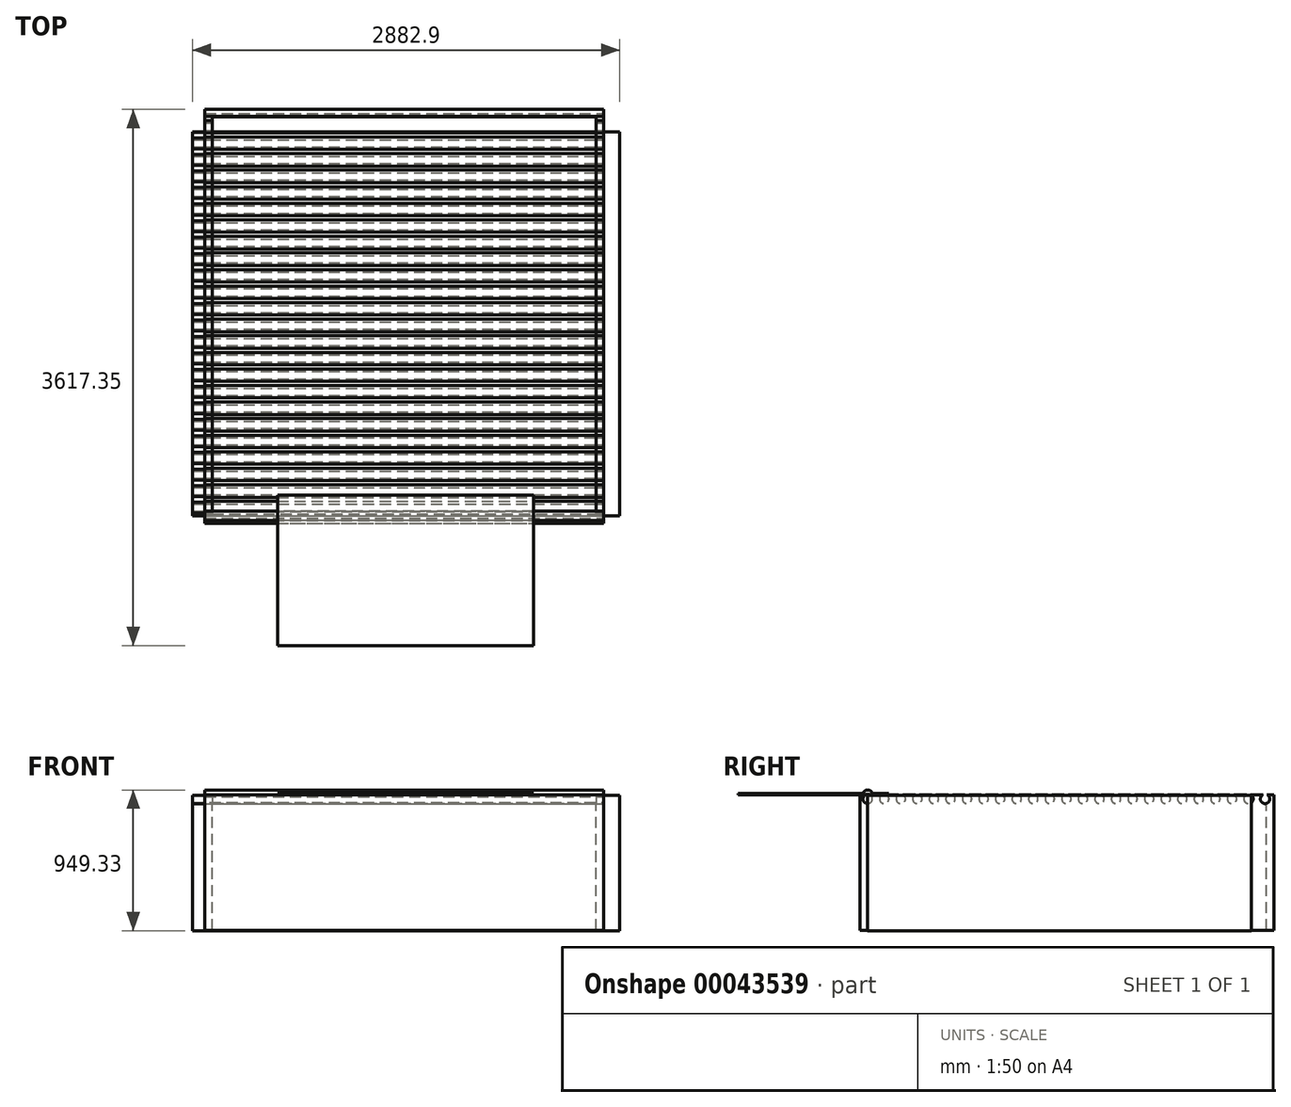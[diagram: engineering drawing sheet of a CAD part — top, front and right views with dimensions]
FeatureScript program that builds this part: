
annotation { "Feature Type Name" : "Feature", "Feature Type Description" : "" }
export const myFeature = defineFeature(function(context is Context, id is Id, definition is map)
    precondition{}
    {
        {
            var Q0;
            Q0=qCreatedBy(makeId("Top.planeOp"),FACE);
            var sketch = newSketch(context, id + "F0", { "sketchPlane" : qUnion([Q0])});
            skLineSegment(sketch, "E0.bottom", {"start": v(-1295.4, 2590.8) * mm, "end": v(1295.4, 2590.8) * mm});
            skLineSegment(sketch, "E0.top", {"start": v(-1295.4, 0) * mm, "end": v(1295.4, 0) * mm});
            skLineSegment(sketch, "E0.left", {"start": v(-1295.4, 2590.8) * mm, "end": v(-1295.4, 0) * mm});
            skLineSegment(sketch, "E0.right", {"start": v(1295.4, 2590.8) * mm, "end": v(1295.4, 0) * mm});
            skSolve(sketch);
        }
        {
            var Q0;
            Q0=makeQuery(id+"F0.imprint","IMPRINT",FACE,{"disambiguationData":[TD([[makeQuery(id+"F0.imprint","IMPRINT",EDGE,{"derivedFrom":sQuery(id+"F0.wireOp",EDGE,"E0.bottom")}),-1.0]])]});
            extrude(context, id + "F1", {"entities" : qUnion([Q0]), "oppositeDirection" : true, "depth" : 3.17 * mm});
        }
        {
            var Q0;
            Q0=makeQuery(id+"F1.opExtrude","CAP_FACE",FACE,{"disambiguationData":[OSD([sQuery(id+"F0.wireOp",EDGE,"E0.bottom"),sQuery(id+"F0.wireOp",EDGE,"E0.top"),sQuery(id+"F0.wireOp",EDGE,"E0.left"),sQuery(id+"F0.wireOp",EDGE,"E0.right")])],"isStart":false});
            var sketch = newSketch(context, id + "F2", { "sketchPlane" : qUnion([Q0])});
            skLineSegment(sketch, "E1.bottom", {"start": v(-1428.75, 0) * mm, "end": v(1454.15, 0) * mm});
            skLineSegment(sketch, "E1.top", {"start": v(-1428.75, -2590.8) * mm, "end": v(1454.15, -2590.8) * mm});
            skLineSegment(sketch, "E1.left", {"start": v(-1428.75, 0) * mm, "end": v(-1428.75, -2590.8) * mm});
            skLineSegment(sketch, "E1.right", {"start": v(1454.15, 0) * mm, "end": v(1454.15, -2590.8) * mm});
            skSolve(sketch);
        }
        {
            var Q0;
            Q0 = qSketchRegion(id + "F2", true);
            extrude(context, id + "F3", {"entities" : qUnion([Q0]), "operationType" : NewBodyOperationType.ADD, "depth" : 914.4 * mm});
        }
        {
            var Q0;
            Q0=qCreatedBy(makeId("Top.planeOp"),FACE);
            var sketch = newSketch(context, id + "F4", { "sketchPlane" : qUnion([Q0])});
            skLineSegment(sketch, "E2.bottom", {"start": v(-1295.4, 2590.8) * mm, "end": v(1295.4, 2590.8) * mm});
            skLineSegment(sketch, "E2.top", {"start": v(-1295.4, 0) * mm, "end": v(1295.4, 0) * mm});
            skLineSegment(sketch, "E2.left", {"start": v(-1295.4, 2590.8) * mm, "end": v(-1295.4, 0) * mm});
            skLineSegment(sketch, "E2.right", {"start": v(1295.4, 2590.8) * mm, "end": v(1295.4, 0) * mm});
            skLineSegment(sketch, "E3.bottom", {"start": v(-1295.4, -25.4) * mm, "end": v(1295.4, -25.4) * mm});
            skLineSegment(sketch, "E3.top", {"start": v(-1295.4, -2819.4) * mm, "end": v(1295.4, -2819.4) * mm});
            skLineSegment(sketch, "E3.left", {"start": v(-1295.4, -25.4) * mm, "end": v(-1295.4, -2819.4) * mm});
            skLineSegment(sketch, "E3.right", {"start": v(1295.4, -25.4) * mm, "end": v(1295.4, -2819.4) * mm});
            skLineSegment(sketch, "E4.0", {"start": v(-1346.2, 25.4) * mm, "end": v(-1346.2, -2870.2) * mm});
            skLineSegment(sketch, "E4.1", {"start": v(-1346.2, 25.4) * mm, "end": v(1346.2, 25.4) * mm});
            skLineSegment(sketch, "E4.2", {"start": v(1346.2, 25.4) * mm, "end": v(1346.2, -2870.2) * mm});
            skLineSegment(sketch, "E4.3", {"start": v(-1346.2, -2870.2) * mm, "end": v(1346.2, -2870.2) * mm});
            skSolve(sketch);
        }
        {
            var Q0;
            {var subQ4=sQuery(id+"F4.wireOp",EDGE,"E2.top");Q0=makeQuery(id+"F4.imprint","IMPRINT",FACE,{"disambiguationData":[TD([[makeQuery(id+"F4.imprint","IMPRINT",EDGE,{"derivedFrom":subQ4}),-1.0]])]});}
            extrude(context, id + "F5", {"entities" : qUnion([Q0]), "oppositeDirection" : true, "depth" : 914.4 * mm});
        }
        {
            var Q0;
            Q0=makeQuery(id+"F5.opExtrude","SWEPT_BODY",BODY,{"disambiguationData":[OSD([sQuery(id+"F4.wireOp",EDGE,"E2.top"),sQuery(id+"F4.wireOp",EDGE,"E2.left"),sQuery(id+"F4.wireOp",EDGE,"E2.right"),sQuery(id+"F4.wireOp",EDGE,"E3.bottom"),sQuery(id+"F4.wireOp",EDGE,"E3.top"),sQuery(id+"F4.wireOp",EDGE,"E3.left"),sQuery(id+"F4.wireOp",EDGE,"E3.right"),sQuery(id+"F4.wireOp",EDGE,"E4.0"),sQuery(id+"F4.wireOp",EDGE,"E4.1"),sQuery(id+"F4.wireOp",EDGE,"E4.2"),sQuery(id+"F4.wireOp",EDGE,"E4.3")])]});
            deleteBodies(context, id + "F6", {"entities" : qUnion([Q0])});
        }
        {
            var Q0;
            Q0=qCreatedBy(makeId("Top.planeOp"),FACE);
            var sketch = newSketch(context, id + "F7", { "sketchPlane" : qUnion([Q0])});
            skLineSegment(sketch, "E5.bottom", {"start": v(-1295.4, 2692.4) * mm, "end": v(1295.4, 2692.4) * mm});
            skLineSegment(sketch, "E5.top", {"start": v(-1295.4, 0) * mm, "end": v(1295.4, 0) * mm});
            skLineSegment(sketch, "E5.left", {"start": v(-1295.4, 2692.4) * mm, "end": v(-1295.4, 0) * mm});
            skLineSegment(sketch, "E5.right", {"start": v(1295.4, 2692.4) * mm, "end": v(1295.4, 0) * mm});
            skLineSegment(sketch, "E6.0", {"start": v(-1346.2, -50.8) * mm, "end": v(1346.2, -50.8) * mm});
            skLineSegment(sketch, "E6.1", {"start": v(-1346.2, 2743.2) * mm, "end": v(-1346.2, -50.8) * mm});
            skLineSegment(sketch, "E6.2", {"start": v(-1346.2, 2743.2) * mm, "end": v(1346.2, 2743.2) * mm});
            skLineSegment(sketch, "E6.3", {"start": v(1346.2, 2743.2) * mm, "end": v(1346.2, -50.8) * mm});
            skSolve(sketch);
        }
        {
            var Q0;
            Q0=makeQuery(id+"F7.imprint","IMPRINT",FACE,{"disambiguationData":[TD([[makeQuery(id+"F7.imprint","IMPRINT",EDGE,{"derivedFrom":sQuery(id+"F7.wireOp",EDGE,"E5.bottom")}),1.0]])]});
            extrude(context, id + "F8", {"entities" : qUnion([Q0]), "oppositeDirection" : true, "depth" : 914.4 * mm});
        }
        {
            var Q0;
            Q0=qCreatedBy(makeId("Right.planeOp"),FACE);
            var sketch = newSketch(context, id + "F9", { "sketchPlane" : qUnion([Q0])});
            skCircle(sketch, "E7", {"center": v(0, 0) * mm, "radius": 31.75 * mm});
            skSolve(sketch);
        }
        {
            var Q0;
            Q0 = qSketchRegion(id + "F9", true);
            extrude(context, id + "F10", {"entities" : qUnion([Q0]), "depth" : 2692.4 * mm, "symmetric" : true});
        }
        {
            var Q0;
            Q0=makeQuery(id+"F8.opExtrude","SWEPT_FACE",FACE,{"disambiguationData":[OSD([sQuery(id+"F7.wireOp",EDGE,"E6.3")])]});
            var sketch = newSketch(context, id + "F11", { "sketchPlane" : qUnion([Q0])});
            skCircle(sketch, "E8", {"center": v(0, -28.58) * mm, "radius": 31.75 * mm});
            skCircle(sketch, "E9.1.0.0", {"center": v(111.76, -28.57) * mm, "radius": 31.75 * mm});
            skCircle(sketch, "E9.2.0.0", {"center": v(223.52, -28.57) * mm, "radius": 31.75 * mm});
            skCircle(sketch, "E9.3.0.0", {"center": v(335.28, -28.57) * mm, "radius": 31.75 * mm});
            skCircle(sketch, "E9.4.0.0", {"center": v(447.04, -28.57) * mm, "radius": 31.75 * mm});
            skCircle(sketch, "E9.5.0.0", {"center": v(558.8, -28.57) * mm, "radius": 31.75 * mm});
            skCircle(sketch, "E9.6.0.0", {"center": v(670.56, -28.57) * mm, "radius": 31.75 * mm});
            skCircle(sketch, "E9.7.0.0", {"center": v(782.32, -28.57) * mm, "radius": 31.75 * mm});
            skCircle(sketch, "E9.8.0.0", {"center": v(894.08, -28.57) * mm, "radius": 31.75 * mm});
            skCircle(sketch, "E9.9.0.0", {"center": v(1005.84, -28.57) * mm, "radius": 31.75 * mm});
            skCircle(sketch, "E9.10.0.0", {"center": v(1117.6, -28.57) * mm, "radius": 31.75 * mm});
            skCircle(sketch, "E9.11.0.0", {"center": v(1229.36, -28.57) * mm, "radius": 31.75 * mm});
            skCircle(sketch, "E9.12.0.0", {"center": v(1341.12, -28.57) * mm, "radius": 31.75 * mm});
            skCircle(sketch, "E9.13.0.0", {"center": v(1452.88, -28.57) * mm, "radius": 31.75 * mm});
            skCircle(sketch, "E9.14.0.0", {"center": v(1564.64, -28.57) * mm, "radius": 31.75 * mm});
            skCircle(sketch, "E9.15.0.0", {"center": v(1676.4, -28.57) * mm, "radius": 31.75 * mm});
            skCircle(sketch, "E9.16.0.0", {"center": v(1788.16, -28.57) * mm, "radius": 31.75 * mm});
            skCircle(sketch, "E9.17.0.0", {"center": v(1899.92, -28.57) * mm, "radius": 31.75 * mm});
            skCircle(sketch, "E9.18.0.0", {"center": v(2011.68, -28.57) * mm, "radius": 31.75 * mm});
            skCircle(sketch, "E9.19.0.0", {"center": v(2123.44, -28.57) * mm, "radius": 31.75 * mm});
            skCircle(sketch, "E9.20.0.0", {"center": v(2235.2, -28.57) * mm, "radius": 31.75 * mm});
            skCircle(sketch, "E9.21.0.0", {"center": v(2346.96, -28.57) * mm, "radius": 31.75 * mm});
            skCircle(sketch, "E9.22.0.0", {"center": v(2458.72, -28.57) * mm, "radius": 31.75 * mm});
            skCircle(sketch, "E9.23.0.0", {"center": v(2570.48, -28.57) * mm, "radius": 31.75 * mm});
            skCircle(sketch, "E9.24.0.0", {"center": v(2682.24, -28.57) * mm, "radius": 31.75 * mm});
            skLineSegment(sketch, "E9.direction1", {"start": v(0, -28.58) * mm, "end": v(111.76, -28.58) * mm, "construction": true});
            skSolve(sketch);
        }
        {
            var Q0;
            Q0 = qSketchRegion(id + "F11", true);
            extrude(context, id + "F12", {"entities" : qUnion([Q0]), "operationType" : NewBodyOperationType.REMOVE, "endBound" : BoundingType.THROUGH_ALL, "oppositeDirection" : true, "depth" : 25.4 * mm});
        }
        {
            var Q0;
            Q0=qCreatedBy(makeId("Top.planeOp"),FACE);
            var sketch = newSketch(context, id + "F13", { "sketchPlane" : qUnion([Q0])});
            skLineSegment(sketch, "E10.bottom", {"start": v(-855.38, -874.15) * mm, "end": v(871.82, -874.15) * mm});
            skLineSegment(sketch, "E10.top", {"start": v(-855.38, 141.85) * mm, "end": v(871.82, 141.85) * mm});
            skLineSegment(sketch, "E10.left", {"start": v(-855.38, -874.15) * mm, "end": v(-855.38, 141.85) * mm});
            skLineSegment(sketch, "E10.right", {"start": v(871.82, -874.15) * mm, "end": v(871.82, 141.85) * mm});
            skSolve(sketch);
        }
        {
            var Q0;
            Q0=makeQuery(id+"F13.imprint","IMPRINT",FACE,{"disambiguationData":[TD([[makeQuery(id+"F13.imprint","IMPRINT",EDGE,{"derivedFrom":sQuery(id+"F13.wireOp",EDGE,"E10.bottom")}),1.0]])]});
            extrude(context, id + "F14", {"entities" : qUnion([Q0]), "depth" : 7.62 * mm});
        }
    });
